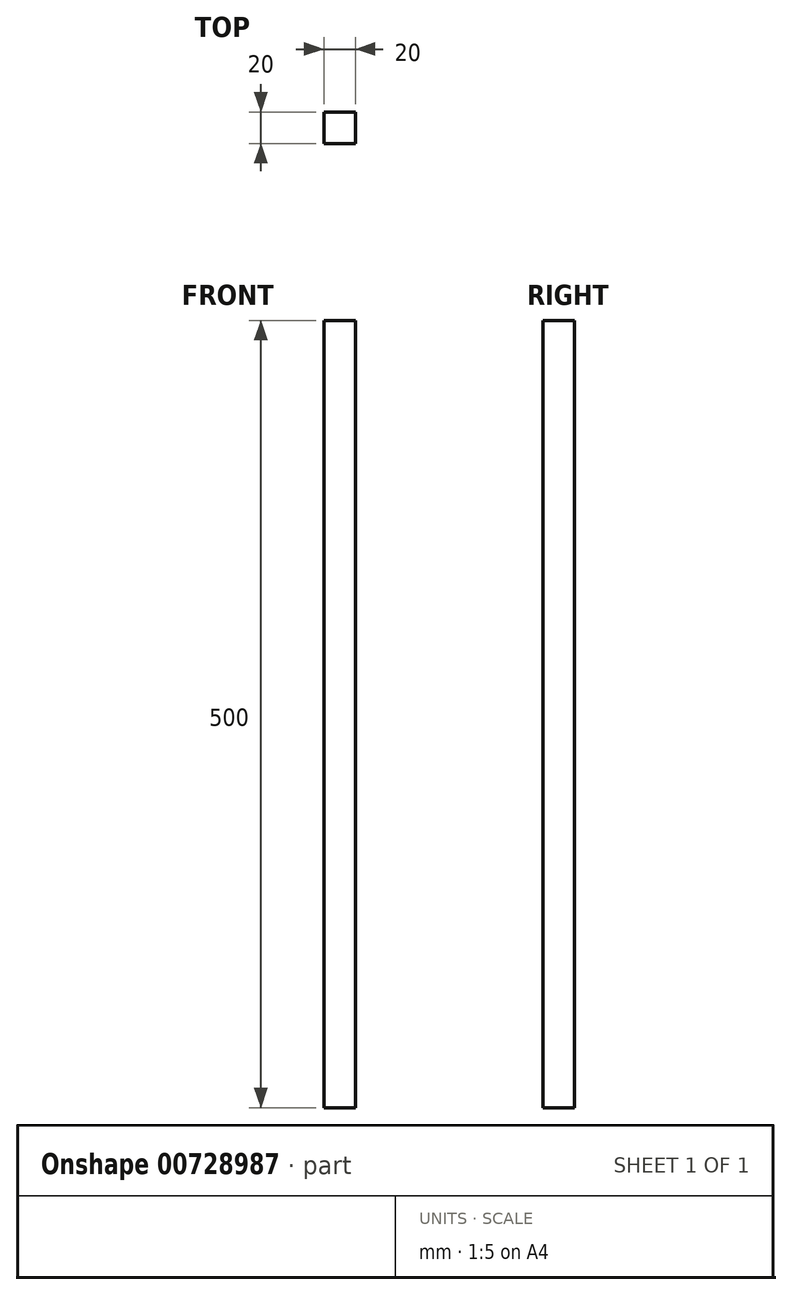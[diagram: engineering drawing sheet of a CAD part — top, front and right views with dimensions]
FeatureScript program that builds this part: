
annotation { "Feature Type Name" : "Feature", "Feature Type Description" : "" }
export const myFeature = defineFeature(function(context is Context, id is Id, definition is map)
    precondition{}
    {
        {
            var Q0;
            Q0=qCreatedBy(makeId("Top.planeOp"),FACE);
            var sketch = newSketch(context, id + "F0", { "sketchPlane" : qUnion([Q0])});
            skLineSegment(sketch, "E0.bottom", {"start": v(10, 10) * mm, "end": v(-10, 10) * mm});
            skLineSegment(sketch, "E0.top", {"start": v(10, -10) * mm, "end": v(-10, -10) * mm});
            skLineSegment(sketch, "E0.left", {"start": v(10, 10) * mm, "end": v(10, -10) * mm});
            skLineSegment(sketch, "E0.right", {"start": v(-10, 10) * mm, "end": v(-10, -10) * mm});
            skPoint(sketch, "E0.middle", {"position": v(0, 0) * mm});
            skSolve(sketch);
        }
        {
            var Q0;
            Q0=makeQuery(id+"F0.imprint","IMPRINT",FACE,{"disambiguationData":[TD([[makeQuery(id+"F0.imprint","IMPRINT",EDGE,{"derivedFrom":sQuery(id+"F0.wireOp",EDGE,"E0.bottom")}),1.0]])]});
            extrude(context, id + "F1", {"entities" : qUnion([Q0]), "depth" : 500 * mm, "offsetDistance" : 25 * mm});
        }
    });
